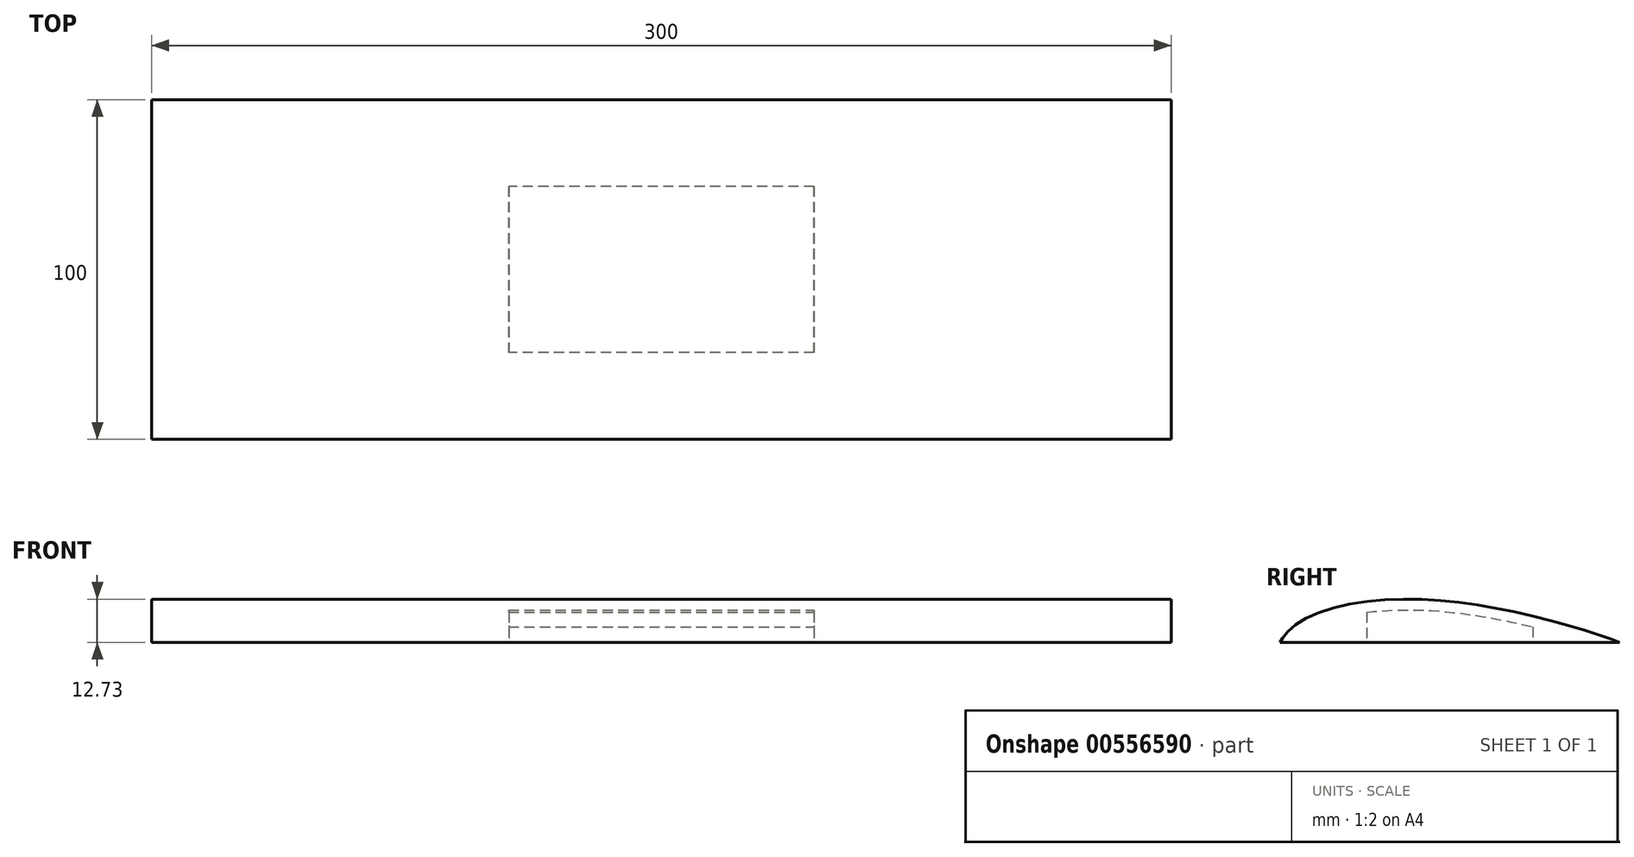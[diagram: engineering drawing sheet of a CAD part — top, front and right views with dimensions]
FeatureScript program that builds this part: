
annotation { "Feature Type Name" : "Feature", "Feature Type Description" : "" }
export const myFeature = defineFeature(function(context is Context, id is Id, definition is map)
    precondition{}
    {
        {
            var Q0;
            Q0=qCreatedBy(makeId("Top.planeOp"),FACE);
            var sketch = newSketch(context, id + "F0", { "sketchPlane" : qUnion([Q0])});
            skLineSegment(sketch, "E0.bottom", {"start": v(-150, 50) * mm, "end": v(150, 50) * mm});
            skLineSegment(sketch, "E0.top", {"start": v(-150, -50) * mm, "end": v(150, -50) * mm});
            skLineSegment(sketch, "E0.left", {"start": v(-150, 50) * mm, "end": v(-150, -50) * mm});
            skLineSegment(sketch, "E0.right", {"start": v(150, 50) * mm, "end": v(150, -50) * mm});
            skPoint(sketch, "E0.middle", {"position": v(0, 0) * mm});
            skSolve(sketch);
        }
        {
            var Q0;
            Q0 = qSketchRegion(id + "F0", true);
            extrude(context, id + "F1", {"entities" : qUnion([Q0]), "depth" : 25 * mm, "offsetDistance" : 25.4 * mm});
        }
        {
            var Q0;
            Q0=makeQuery(id+"F1.opExtrude","SWEPT_FACE",FACE,{"disambiguationData":[OSD([sQuery(id+"F0.wireOp",EDGE,"E0.right")])]});
            var sketch = newSketch(context, id + "F2", { "sketchPlane" : qUnion([Q0])});
            skFitSpline(sketch, "E1", {"points": [v(-50, 0) * mm, v(-44.6, 5.73) * mm, v(-15.9, 12.67) * mm, v(24.57, 7.68) * mm, v(50, 0) * mm], "startDerivative": vector(11.37, 17.48) * mm, "endDerivative": vector(45.88, -20.19) * mm});
            skSolve(sketch);
        }
        {
            var Q0;
            Q0 = qSketchRegion(id + "F2", true);
            var Q1;
            Q1=makeQuery(id+"F2.imprint","IMPRINT",FACE,{"disambiguationData":[TD([[makeQuery(id+"F2.imprint","IMPRINT",EDGE,{"derivedFrom":sQuery(id+"F2.wireOp",EDGE,"E1")}),1.0]])]});
            extrude(context, id + "F3", {"entities" : qUnion([Q0, Q1]), "operationType" : NewBodyOperationType.REMOVE, "endBound" : BoundingType.THROUGH_ALL, "oppositeDirection" : true, "depth" : 25.4 * mm, "offsetDistance" : 25.4 * mm});
        }
        {
            var Q0;
            Q0=makeQuery(id+"F1.opExtrude","CAP_FACE",FACE,{"disambiguationData":[OSD([sQuery(id+"F0.wireOp",EDGE,"E0.bottom"),sQuery(id+"F0.wireOp",EDGE,"E0.top"),sQuery(id+"F0.wireOp",EDGE,"E0.left"),sQuery(id+"F0.wireOp",EDGE,"E0.right")])],"isStart":true});
            var sketch = newSketch(context, id + "F4", { "sketchPlane" : qUnion([Q0])});
            skLineSegment(sketch, "E2.bottom", {"start": v(-190.5, 76.2) * mm, "end": v(190.5, 76.2) * mm});
            skLineSegment(sketch, "E2.top", {"start": v(-190.5, -76.2) * mm, "end": v(190.5, -76.2) * mm});
            skLineSegment(sketch, "E2.left", {"start": v(-190.5, 76.2) * mm, "end": v(-190.5, -76.2) * mm});
            skLineSegment(sketch, "E2.right", {"start": v(190.5, 76.2) * mm, "end": v(190.5, -76.2) * mm});
            skLineSegment(sketch, "E3", {"start": v(-190.5, 76.2) * mm, "end": v(190.5, -76.2) * mm, "construction": true});
            skLineSegment(sketch, "E4.0.0", {"start": v(-150, 50) * mm, "end": v(-150, -50) * mm});
            skLineSegment(sketch, "E4.0.1", {"start": v(-150, -50) * mm, "end": v(150, -50) * mm});
            skLineSegment(sketch, "E4.0.2", {"start": v(150, -50) * mm, "end": v(150, 50) * mm});
            skLineSegment(sketch, "E4.0.3", {"start": v(150, 50) * mm, "end": v(-150, 50) * mm});
            skLineSegment(sketch, "E5.0", {"start": v(156.35, 56.35) * mm, "end": v(-156.35, 56.35) * mm});
            skLineSegment(sketch, "E5.1", {"start": v(156.35, -56.35) * mm, "end": v(156.35, 56.35) * mm});
            skLineSegment(sketch, "E5.2", {"start": v(-156.35, -56.35) * mm, "end": v(156.35, -56.35) * mm});
            skLineSegment(sketch, "E5.3", {"start": v(-156.35, 56.35) * mm, "end": v(-156.35, -56.35) * mm});
            skSolve(sketch);
        }
        {
            var Q0;
            Q0=makeQuery(id+"FK7JJDqbAfnstOU_1.opExtrude","CAP_FACE",FACE,{"disambiguationData":[OSD([sQuery(id+"F4.wireOp",EDGE,"E2.bottom"),sQuery(id+"F4.wireOp",EDGE,"E2.top"),sQuery(id+"F4.wireOp",EDGE,"E2.left"),sQuery(id+"F4.wireOp",EDGE,"E2.right"),sQuery(id+"F4.wireOp",EDGE,"E5.0"),sQuery(id+"F4.wireOp",EDGE,"E5.1"),sQuery(id+"F4.wireOp",EDGE,"E5.2"),sQuery(id+"F4.wireOp",EDGE,"E5.3")])],"isStart":true});
            var sketch = newSketch(context, id + "F5", { "sketchPlane" : qUnion([Q0])});
            skLineSegment(sketch, "E6.0.0", {"start": v(-190.5, 76.2) * mm, "end": v(-190.5, -76.2) * mm});
            skLineSegment(sketch, "E6.0.1", {"start": v(-190.5, -76.2) * mm, "end": v(190.5, -76.2) * mm});
            skLineSegment(sketch, "E6.0.2", {"start": v(190.5, -76.2) * mm, "end": v(190.5, 76.2) * mm});
            skLineSegment(sketch, "E6.0.3", {"start": v(190.5, 76.2) * mm, "end": v(-190.5, 76.2) * mm});
            skSolve(sketch);
        }
        {
            var Q0;
            Q0=makeQuery(id+"F4.imprint","IMPRINT",FACE,{"disambiguationData":[TD([[makeQuery(id+"F4.imprint","IMPRINT",EDGE,{"derivedFrom":sQuery(id+"F4.wireOp",EDGE,"E4.0.0")}),-1.0]])]});
            var sketch = newSketch(context, id + "F6", { "sketchPlane" : qUnion([Q0])});
            skLineSegment(sketch, "E7.bottom", {"start": v(44.94, -24.45) * mm, "end": v(-44.94, -24.45) * mm});
            skLineSegment(sketch, "E7.top", {"start": v(44.94, 24.45) * mm, "end": v(-44.94, 24.45) * mm});
            skLineSegment(sketch, "E7.left", {"start": v(44.94, -24.45) * mm, "end": v(44.94, 24.45) * mm});
            skLineSegment(sketch, "E7.right", {"start": v(-44.94, -24.45) * mm, "end": v(-44.94, 24.45) * mm});
            skPoint(sketch, "E7.middle", {"position": v(0, 0) * mm});
            skSolve(sketch);
        }
        {
            var Q0;
            Q0 = qSketchRegion(id + "F6", true);
            var Q1;
            Q1=makeQuery(id+"F3.boolean.opBoolean","COPY",FACE,{"derivedFrom":makeQuery(id+"F3.opExtrude","SWEPT_FACE",FACE,{"disambiguationData":[OSD([sQuery(id+"F2.wireOp",EDGE,"E1")])]})});
            extrude(context, id + "F7", {"entities" : qUnion([Q0]), "operationType" : NewBodyOperationType.REMOVE, "endBound" : BoundingType.UP_TO_SURFACE, "oppositeDirection" : true, "depth" : 25.4 * mm, "endBoundEntityFace" : qUnion([Q1]), "hasOffset" : true, "offsetDistance" : 3.17 * mm});
        }
    });
